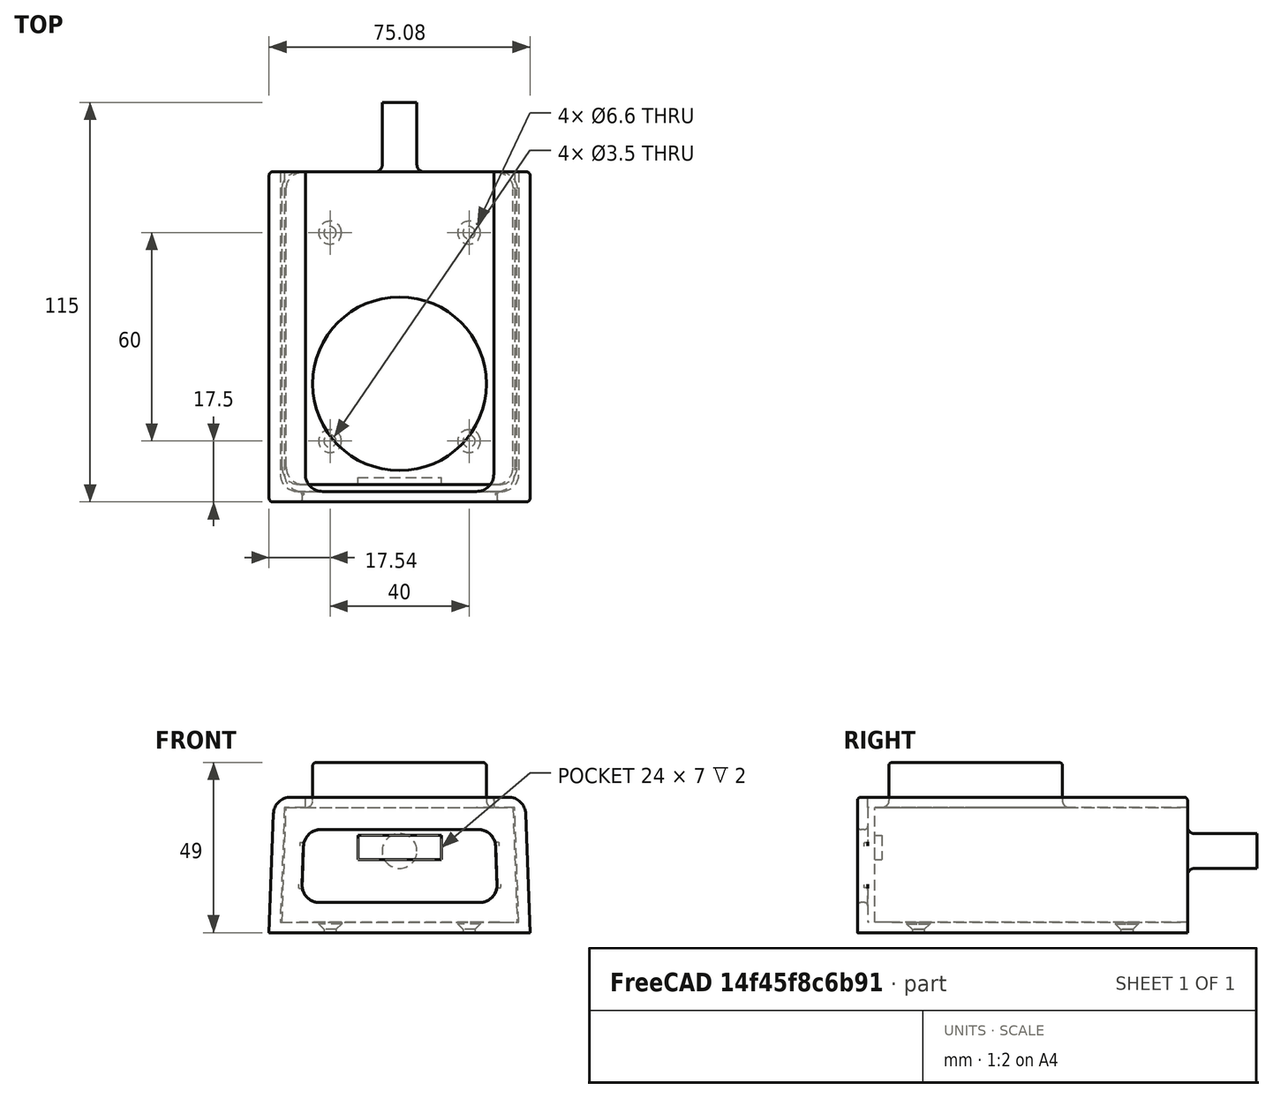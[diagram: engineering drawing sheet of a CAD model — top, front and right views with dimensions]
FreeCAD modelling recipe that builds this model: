
FCSTD DOCUMENT  (FreeCAD 0.22R37100 (Git))
Label: Tågvirke Mount
License: All rights reserved
LicenseURL: http://en.wikipedia.org/wiki/All_rights_reserved
objects: TechDraw::DrawViewDimension×9, Sketcher::SketchObject×7, PartDesign::Fillet×6, PartDesign::Pad×5, TechDraw::DrawViewPart×3, PartDesign::Body×2, PartDesign::SubShapeBinder×2, PartDesign::Pocket×1, PartDesign::Hole×1, TechDraw::DrawSVGTemplate×1, TechDraw::DrawViewImage×1, TechDraw::DrawPage×1
note: 53 computed .brp shape members not serialized (recipe doc carries the construction recipe); baked Part::Feature solids carry a one-line shape summary decoded from their .brp

FEATURE [Sketcher::SketchObject] Sketch
  AttachmentSupport = -> [XZ_Plane]
  FullyConstrained = true
  MapMode = 5
  Placement = pos=(0,0,0) rot=(1,0,0;1.5708rad)
  sketch-geometry (4):
    g0: LineSegment StartX=-32.625 StartY=33 StartZ=0 EndX=32.625 EndY=33 EndZ=0
    g1: LineSegment StartX=32.625 StartY=33 StartZ=0 EndX=33.825 EndY=1e-15 EndZ=0
    g2: LineSegment StartX=33.825 StartY=1e-15 StartZ=0 EndX=-33.825 EndY=0 EndZ=0
    g3: LineSegment StartX=-33.825 StartY=0 StartZ=0 EndX=-32.625 EndY=33 EndZ=0
  constraints (10):
    c: Coincident(g0,g1)
    c: Coincident(g1,g2)
    c: Coincident(g2,g3)
    c: Coincident(g3,g0)
    c: PointOnObject(g1,g-1)
    c: Symmetric(g0,g0,g-2)
    c: DistanceX(g0,g0) = 65.25
    c: DistanceX(g2,g2) = 67.65
    c: Symmetric(g2,g1,g-2)
    c: DistanceY(g1,g0) = 33
FEATURE [PartDesign::Pad] Pad
  Direction = (0,-1,2e-16)
  Length = 90
  Length2 = 10
  Placement = pos=(0,0,0) rot=(1,0,0;1.5708rad)
  Profile = -> Sketch
  ReferenceAxis = -> Sketch [N_Axis]
  Reversed = true
  Suppressed = false
  Type = 0
FEATURE [Sketcher::SketchObject] Sketch001
  AttachmentSupport = -> [Pad]
  FullyConstrained = true
  MapMode = 5
  Placement = pos=(0,0,0) rot=(1,0,0;1.5708rad)
  sketch-geometry (4):
    g0: LineSegment StartX=-12 StartY=25 StartZ=0 EndX=12 EndY=25 EndZ=0
    g1: LineSegment StartX=12 StartY=25 StartZ=0 EndX=12 EndY=18 EndZ=0
    g2: LineSegment StartX=12 StartY=18 StartZ=0 EndX=-12 EndY=18 EndZ=0
    g3: LineSegment StartX=-12 StartY=18 StartZ=0 EndX=-12 EndY=25 EndZ=0
  constraints (11):
    c: Coincident(g0,g1)
    c: Coincident(g1,g2)
    c: Coincident(g2,g3)
    c: Coincident(g3,g0)
    c: Horizontal(g2)
    c: Vertical(g1)
    c: Vertical(g3)
    c: DistanceX(g0,g0) = 24
    c: DistanceY(g1,g1) = 7
    c: Symmetric(g0,g0,g-2)
    c: DistanceY(g-1,g1) = 18
FEATURE [PartDesign::Pocket] Pocket
  BaseFeature = -> Pad
  Direction = (0,1,-2e-16)
  Length = 2
  Length2 = 5
  Placement = pos=(0,0,0) rot=(1,0,0;1.5708rad)
  Profile = -> Sketch001
  ReferenceAxis = -> Sketch001 [N_Axis]
  Suppressed = false
  Type = 0
FEATURE [Sketcher::SketchObject] Sketch002
  AttachmentSupport = -> [Pocket]
  FullyConstrained = true
  MapMode = 5
  Placement = pos=(0,1.45e-14,33) rot=(0,0,1;3.14159rad)
  sketch-geometry (1):
    g0: Circle CenterX=0 CenterY=-29 CenterZ=0 NormalX=0 NormalY=0 NormalZ=1 AngleXU=0 Radius=25
  constraints (3):
    c: PointOnObject(g0,g-2)
    c: Diameter(g0) = 50
    c: DistanceY(g0,g-1) = 29
FEATURE [PartDesign::Pad] Pad001
  BaseFeature = -> Pocket
  Direction = (0,2e-16,1)
  Length = 13
  Length2 = 10
  Placement = pos=(0,0,0) rot=(1,0,0;1.5708rad)
  Profile = -> Sketch002
  ReferenceAxis = -> Sketch002 [N_Axis]
  Suppressed = false
  Type = 0
FEATURE [PartDesign::Fillet] Fillet
  Base = -> Pad001 [Edge19]
  BaseFeature = -> Pad001
  Placement = pos=(0,0,0) rot=(1,0,0;1.5708rad)
  Radius = 1
  SupportTransform = false
  Suppressed = false
  UseAllEdges = false
FEATURE [PartDesign::Fillet] Fillet001
  Base = -> Fillet [Edge3]
  BaseFeature = -> Fillet
  Placement = pos=(0,0,0) rot=(1,0,0;1.5708rad)
  Radius = 2
  SupportTransform = false
  Suppressed = false
  UseAllEdges = false
FEATURE [PartDesign::Fillet] Fillet002
  Base = -> Fillet001 [Edge15,Edge21,Edge13,Edge14]
  BaseFeature = -> Fillet001
  Placement = pos=(0,0,0) rot=(1,0,0;1.5708rad)
  Radius = 5
  SupportTransform = false
  Suppressed = false
  UseAllEdges = false
FEATURE [Sketcher::SketchObject] Sketch003
  AttachmentSupport = -> [Fillet002]
  FullyConstrained = true
  MapMode = 5
  Placement = pos=(0,90,-1.98e-14) rot=(-1,0,0;1.5708rad)
  sketch-geometry (1):
    g0: Circle CenterX=0 CenterY=-20.5 CenterZ=0 NormalX=0 NormalY=0 NormalZ=1 AngleXU=0 Radius=5
  constraints (3):
    c: PointOnObject(g0,g-2)
    c: Diameter(g0) = 10
    c: DistanceY(g0,g-1) = 20.5
FEATURE [PartDesign::Pad] Pad002
  BaseFeature = -> Fillet002
  Direction = (0,1,-2e-16)
  Length = 20
  Length2 = 10
  Placement = pos=(0,0,0) rot=(1,0,0;1.5708rad)
  Profile = -> Sketch003
  ReferenceAxis = -> Sketch003 [N_Axis]
  Suppressed = false
  Type = 0
FEATURE [PartDesign::Fillet] Fillet003
  Base = -> Pad002 [Edge25]
  BaseFeature = -> Pad002
  Placement = pos=(0,0,0) rot=(1,0,0;1.5708rad)
  Radius = 2
  SupportTransform = false
  Suppressed = false
  UseAllEdges = false
FEATURE [PartDesign::Body] Body  label="Tågvirke"
  Group = -> [Sketch,Pad,Sketch001,Pocket,Sketch002,Pad001,Fillet,Fillet001,Fillet002,Sketch003,Pad002,Fillet003]
  Origin = -> Origin
  Tip = -> Fillet003
FEATURE [PartDesign::SubShapeBinder] Binder  label="Port Binder"
  BindCopyOnChange = 0
  BindMode = 0
  ClaimChildren = false
  Context = -> Body001 [Binder.]
  Fuse = false
  MakeFace = true
  OffsetFill = false
  OffsetIntersection = false
  OffsetJoinType = 0
  OffsetOpenResult = false
  PartialLoad = false
  Relative = true
  Support = -> [Body[Fillet001.Face7]]
  _Version = 2
FEATURE [PartDesign::SubShapeBinder] Binder001  label="Top Binder"
  BindCopyOnChange = 0
  BindMode = 0
  ClaimChildren = false
  Context = -> Body001 [Binder001.]
  Fuse = false
  MakeFace = true
  OffsetFill = false
  OffsetIntersection = false
  OffsetJoinType = 0
  OffsetOpenResult = false
  PartialLoad = false
  Relative = true
  Support = -> [Body[Fillet001.Face4]]
  _Version = 2
FEATURE [Sketcher::SketchObject] Sketch004  label="side_walls"
  AttachmentSupport = -> [XZ_Plane001]
  ExternalGeometry = -> [Binder]
  FullyConstrained = true
  MapMode = 5
  Placement = pos=(0,0,0) rot=(1,0,0;1.5708rad)
  expr: Constraints[27] = .Constraints.wall_thickness
  expr: Constraints[30] = .Constraints.wall_thickness
  sketch-geometry (12):
    g0: LineSegment StartX=-27.125 StartY=33 StartZ=0 EndX=-33.125 EndY=33 EndZ=0
    g1: LineSegment StartX=-33.125 StartY=33 StartZ=0 EndX=-34.325 EndY=1e-15 EndZ=0
    g2: LineSegment StartX=-34.325 StartY=1e-15 StartZ=0 EndX=34.325 EndY=0 EndZ=0
    g3: LineSegment StartX=34.325 StartY=0 StartZ=0 EndX=33.125 EndY=33 EndZ=0
    g4: LineSegment StartX=33.125 StartY=33 StartZ=0 EndX=27.125 EndY=33 EndZ=0
    g5: LineSegment StartX=-27.125 StartY=33 StartZ=0 EndX=-27.125 EndY=36 EndZ=0
    g6: LineSegment StartX=-27.125 StartY=36 StartZ=0 EndX=-36.125 EndY=36 EndZ=0
    g7: LineSegment StartX=-36.125 StartY=36 StartZ=0 EndX=-37.5432 EndY=-3 EndZ=0
    g8: LineSegment StartX=-37.5432 StartY=-3 StartZ=0 EndX=37.5432 EndY=-3 EndZ=0
    g9: LineSegment StartX=37.5432 StartY=-3 StartZ=0 EndX=36.125 EndY=36 EndZ=0
    g10: LineSegment StartX=36.125 StartY=36 StartZ=0 EndX=27.125 EndY=36 EndZ=0
    g11: LineSegment StartX=27.125 StartY=36 StartZ=0 EndX=27.125 EndY=33 EndZ=0
  constraints (31):
    c: Horizontal(g0)
    c: Coincident(g1,g2)
    c: Coincident(g2,g3)
    c: Coincident(g3,g4)
    c: DistanceX(g1,g-4) = 0.5  'Back Side Gap'
    c: Symmetric(g1,g2,g-2)
    c: DistanceX(g0,g-5) = 0.5  'Top Side Gap'
    c: Coincident(g0,g1)
    c: Symmetric(g0,g4,g-2)
    c: Symmetric(g0,g3,g-2)
    c: DistanceY(g-5,g0) = 0  'Outter Gap'
    c: DistanceY(g1,g-5) = 0  'Inner Gap'
    c: DistanceX(g0,g0) = 6  'Outter Catch'
    c: Coincident(g0,g5)
    c: Vertical(g5)
    c: Coincident(g5,g6)
    c: Horizontal(g6)
    c: Coincident(g6,g7)
    c: Coincident(g7,g8)
    c: Coincident(g8,g9)
    c: Coincident(g9,g10)
    c: Horizontal(g10)
    c: Coincident(g10,g11)
    c: Coincident(g11,g4)
    c: Vertical(g11)
    c: Symmetric(g9,g6,g-2)
    c: Symmetric(g7,g8,g-2)
    c: DistanceX(g3,g9) = 3
    c: Parallel(g3,g9)
    c: DistanceY(g4,g10) = 3  'wall_thickness'
    c: DistanceY(g8,g2) = 3
FEATURE [PartDesign::Pad] Pad003  label="Side Walls Pad"
  Direction = (0,-1,-2e-16)
  Length = 90
  Length2 = 2
  Placement = pos=(0,0,0) rot=(1,0,0;1.5708rad)
  Profile = -> Sketch004
  ReferenceAxis = -> Sketch004 [N_Axis]
  Reversed = true
  Suppressed = false
  Type = 4
FEATURE [Sketcher::SketchObject] Sketch005  label="end_plate"
  AttachmentSupport = -> [Pad003]
  ExternalGeometry = -> [Pad003]
  FullyConstrained = true
  MapMode = 5
  Placement = pos=(0,-2,-4e-16) rot=(1,0,0;1.5708rad)
  sketch-geometry (11):
    g0: LineSegment StartX=36.125 StartY=36 StartZ=0 EndX=37.5432 EndY=-3 EndZ=0
    g1: LineSegment StartX=37.5432 StartY=-3 StartZ=0 EndX=-37.5432 EndY=-3 EndZ=0
    g2: LineSegment StartX=-37.5432 StartY=-3 StartZ=0 EndX=-36.125 EndY=36 EndZ=0
    g3: LineSegment StartX=-28.2282 StartY=5.66127 StartZ=0 EndX=28.2282 EndY=5.66127 EndZ=0
    g4: LineSegment StartX=28.2282 StartY=5.66127 StartZ=0 EndX=37.5432 EndY=-3 EndZ=0
    g5: LineSegment StartX=-27.4637 StartY=26.685 StartZ=0 EndX=-28.2282 EndY=5.66127 EndZ=0
    g6: LineSegment StartX=28.2282 StartY=5.66127 StartZ=0 EndX=27.4637 EndY=26.685 EndZ=0
    g7: LineSegment StartX=-27.4637 StartY=26.685 StartZ=0 EndX=27.4637 EndY=26.685 EndZ=0
    g8: LineSegment StartX=36.125 StartY=36 StartZ=0 EndX=27.4637 EndY=26.685 EndZ=0
    g9: LineSegment StartX=-36.125 StartY=36 StartZ=0 EndX=36.125 EndY=36 EndZ=0
    g10: LineSegment StartX=27.125 StartY=36 StartZ=0 EndX=27.4637 EndY=26.685 EndZ=0
  constraints (25):
    c: Coincident(g0,g-6)
    c: Coincident(g0,g1)
    c: Coincident(g1,g-7)
    c: Coincident(g1,g2)
    c: Coincident(g5,g3)
    c: Horizontal(g3)
    c: Coincident(g3,g6)
    c: Coincident(g4,g3)
    c: Coincident(g4,g0)
    c: Angle(g0,g4) = 0.785398
    c: Parallel(g5,g2)
    c: Parallel(g6,g0)
    c: Coincident(g7,g6)
    c: Coincident(g8,g0)
    c: Coincident(g8,g6)
    c: Angle(g8,g0) = 0.785398
    c: Coincident(g5,g7)
    c: Coincident(g9,g2)
    c: Coincident(g9,g0)
    c: Coincident(g2,g-7)
    c: Coincident(g0,g-5)
    c: Coincident(g10,g-4)
    c: Coincident(g10,g6)
    c: Parallel(g10,g0)
    c: Symmetric(g5,g6,g-2)
FEATURE [PartDesign::Pad] Pad004  label="End Plate Pad"
  BaseFeature = -> Pad003
  Direction = (0,-1,-2e-16)
  Length = 3
  Length2 = 10
  Placement = pos=(0,0,0) rot=(1,0,0;1.5708rad)
  Profile = -> Sketch005
  ReferenceAxis = -> Sketch005 [N_Axis]
  Suppressed = false
  Type = 0
FEATURE [Sketcher::SketchObject] Sketch006  label="screw_holes"
  AttachmentSupport = -> [Pad004]
  ExternalGeometry = -> [Pad004]
  FullyConstrained = true
  MapMode = 5
  Placement = pos=(0,0,6e-16) rot=(0,0,1;3.14159rad)
  sketch-geometry (12):
    g0: Circle CenterX=-20 CenterY=-12.5 CenterZ=0 NormalX=0 NormalY=0 NormalZ=1 AngleXU=0 Radius=2
    g1: LineSegment StartX=-20 StartY=-12.5 StartZ=0 EndX=20 EndY=-12.5 EndZ=0
    g2: LineSegment StartX=20 StartY=-12.5 StartZ=0 EndX=20 EndY=-72.5 EndZ=0
    g3: LineSegment StartX=20 StartY=-72.5 StartZ=0 EndX=-20 EndY=-72.5 EndZ=0
    g4: LineSegment StartX=-20 StartY=-72.5 StartZ=0 EndX=-20 EndY=-12.5 EndZ=0
    g5: Circle CenterX=20 CenterY=-12.5 CenterZ=0 NormalX=0 NormalY=0 NormalZ=1 AngleXU=0 Radius=2
    g6: Circle CenterX=20 CenterY=-72.5 CenterZ=0 NormalX=0 NormalY=0 NormalZ=1 AngleXU=0 Radius=2
    g7: Circle CenterX=-20 CenterY=-72.5 CenterZ=0 NormalX=0 NormalY=0 NormalZ=1 AngleXU=0 Radius=2
    g8: GeomPoint X=0 Y=-42.5 Z=0
    g9: GeomPoint X=0 Y=5 Z=0
    g10: GeomPoint X=0 Y=-90 Z=0
    g11: LineSegment StartX=20 StartY=-42.5 StartZ=0 EndX=-20 EndY=-42.5 EndZ=0
  constraints (27):
    c: Diameter(g0) = 4
    c: Coincident(g1,g2)
    c: Coincident(g2,g3)
    c: Coincident(g3,g4)
    c: Coincident(g4,g1)
    c: Horizontal(g3)
    c: Vertical(g2)
    c: Vertical(g4)
    c: Coincident(g0,g1)
    c: Coincident(g5,g1)
    c: Coincident(g6,g2)
    c: Coincident(g7,g3)
    c: Symmetric(g0,g5,g-2)
    c: Equal(g0,g5)
    c: Equal(g5,g6)
    c: Equal(g6,g7)
    c: DistanceX(g1,g1) = 40
    c: DistanceY(g2,g2) = 60
    c: PointOnObject(g8,g-2)
    c: PointOnObject(g9,g-3)
    c: PointOnObject(g9,g-2)
    c: PointOnObject(g10,g-4)
    c: Symmetric(g10,g9,g8)
    c: Horizontal(g11)
    c: PointOnObject(g8,g11)
    c: PointOnObject(g11,g4)
    c: Symmetric(g5,g6,g11)
FEATURE [PartDesign::Hole] Hole  label="Holes"
  BaseFeature = -> Pad004
  CustomThreadClearance = 0
  Depth = 256.977
  DepthType = 1
  Diameter = 3.5
  DrillForDepth = false
  DrillPoint = 1
  DrillPointAngle = 118
  HoleCutCountersinkAngle = 90
  HoleCutCustomValues = false
  HoleCutDepth = 0.5
  HoleCutDiameter = 6.6
  HoleCutType = 3
  ModelThread = false
  Placement = pos=(0,0,0) rot=(1,0,0;1.5708rad)
  Profile = -> Sketch006
  Suppressed = false
  Tapered = true
  TaperedAngle = 90
  ThreadClass = 0
  ThreadDepth = 256.977
  ThreadDepthType = 0
  ThreadDirection = 0
  ThreadFit = 0
  ThreadSize = 0
  ThreadType = 0
  Threaded = false
  UseCustomThreadClearance = false
FEATURE [PartDesign::Fillet] Fillet004  label="Large Fillets"
  Base = -> Hole [Edge29,Edge39,Edge56,Edge58,Edge54,Edge53,Edge22,Edge10,Edge7,Edge24]
  BaseFeature = -> Hole
  Placement = pos=(0,0,0) rot=(1,0,0;1.5708rad)
  Radius = 5
  SupportTransform = false
  Suppressed = false
  UseAllEdges = false
FEATURE [PartDesign::Fillet] Fillet005  label="Small Fillets"
  Base = -> Fillet004 [Edge20,Edge16,Edge98,Edge110,Edge77,Edge94,Edge39]
  BaseFeature = -> Fillet004
  Placement = pos=(0,0,0) rot=(1,0,0;1.5708rad)
  Radius = 1
  SupportTransform = false
  Suppressed = false
  UseAllEdges = false
FEATURE [PartDesign::Body] Body001  label="Mount"
  Group = -> [Binder,Binder001,Sketch004,Pad003,Sketch005,Pad004,Sketch006,Hole,Fillet004,Fillet005]
  Origin = -> Origin001
  Tip = -> Fillet005
FEATURE [TechDraw::DrawSVGTemplate] Template
  Height = 210
  Orientation = 1
  Template = /Applications/FreeCAD.app/Contents/Resources/share/Mod/TechDraw/Templates/A4_Landscape_blank.svg
  Width = 297
FEATURE [TechDraw::DrawViewPart] View  label="Bottom"
  CoarseView = false
  Direction = (0,-1,0)
  Focus = 100
  HardHidden = false
  IsoCount = 0
  IsoHidden = false
  IsoVisible = false
  LockPosition = false
  Perspective = false
  Rotation = 0
  ScaleType = 0
  ScrubCount = 0
  SeamHidden = false
  SeamVisible = false
  SmoothHidden = false
  SmoothVisible = true
  Source = -> [Fillet005]
  X = 58.4217
  XDirection = (1,0,0)
  Y = 53.6321
FEATURE [TechDraw::DrawViewPart] View001  label="Back"
  CoarseView = false
  Direction = (0,0,1)
  Focus = 100
  HardHidden = false
  IsoCount = 0
  IsoHidden = false
  IsoVisible = false
  LockPosition = false
  Perspective = false
  Rotation = 0
  ScaleType = 0
  ScrubCount = 0
  SeamHidden = false
  SeamVisible = false
  SmoothHidden = false
  SmoothVisible = true
  Source = -> [Fillet005]
  X = 248.33
  XDirection = (1,0,0)
  Y = 81.2389
FEATURE [TechDraw::DrawViewPart] View002  label="Side"
  CoarseView = false
  Direction = (1,0,0)
  Focus = 100
  HardHidden = false
  IsoCount = 0
  IsoHidden = false
  IsoVisible = false
  LockPosition = false
  Perspective = false
  Rotation = 0
  ScaleType = 0
  ScrubCount = 0
  SeamHidden = false
  SeamVisible = false
  SmoothHidden = false
  SmoothVisible = true
  Source = -> [Fillet005]
  X = 150.898
  XDirection = (0,1,0)
  Y = 53.3126
FEATURE [TechDraw::DrawViewDimension] Dimension
  AngleOverride = false
  Arbitrary = false
  ArbitraryTolerances = false
  BoxCorners = (2) [(-37.5432,-19.5,-1e-07),(37.5432,19.5,1e-07)]
  EqualTolerance = true
  ExtensionAngle = 0
  FormatSpec = %.2w
  FormatSpecOverTolerance = %+.2w
  FormatSpecUnderTolerance = %+.2w
  Inverted = false
  LineAngle = 0
  LockPosition = false
  MeasureType = 1
  OverTolerance = 0
  References2D = -> [View]
  Rotation = 0
  ScaleType = 0
  TheoreticalExact = false
  Type = 1
  UnderTolerance = 0
  X = -1.5857
  Y = -31.9096
FEATURE [TechDraw::DrawViewDimension] Dimension001
  AngleOverride = false
  Arbitrary = false
  ArbitraryTolerances = false
  BoxCorners = (2) [(-37.5432,-19.5,-1e-07),(37.5432,19.5,1e-07)]
  EqualTolerance = true
  ExtensionAngle = 0
  FormatSpec = ⌀%.2w
  FormatSpecOverTolerance = %+.2w
  FormatSpecUnderTolerance = %+.2w
  Inverted = false
  LineAngle = 0
  LockPosition = false
  MeasureType = 1
  OverTolerance = 0
  References2D = -> [View]
  Rotation = 0
  ScaleType = 0
  TheoreticalExact = false
  Type = 5
  UnderTolerance = 0
  X = -39.8075
  Y = 32.2596
FEATURE [TechDraw::DrawViewDimension] Dimension002
  AngleOverride = false
  Arbitrary = false
  ArbitraryTolerances = false
  BoxCorners = (2) [(-37.5432,-19.5,-1e-07),(37.5432,19.5,1e-07)]
  EqualTolerance = true
  ExtensionAngle = 0
  FormatSpec = %.2w
  FormatSpecOverTolerance = %+.2w
  FormatSpecUnderTolerance = %+.2w
  Inverted = false
  LineAngle = 0
  LockPosition = false
  MeasureType = 1
  OverTolerance = 0
  References2D = -> [View]
  Rotation = 0
  ScaleType = 0
  TheoreticalExact = false
  Type = 2
  UnderTolerance = 0
  X = -47.1899
  Y = 1.69222
FEATURE [TechDraw::DrawViewDimension] Dimension003
  AngleOverride = false
  Arbitrary = false
  ArbitraryTolerances = false
  BoxCorners = (2) [(-37.5432,-19.5,-1e-07),(37.5432,19.5,1e-07)]
  EqualTolerance = true
  ExtensionAngle = 0
  FormatSpec = %.2w
  FormatSpecOverTolerance = %+.2w
  FormatSpecUnderTolerance = %+.2w
  Inverted = false
  LineAngle = 0
  LockPosition = false
  MeasureType = 1
  OverTolerance = 0
  References2D = -> [View]
  Rotation = 0
  ScaleType = 0
  TheoreticalExact = false
  Type = 1
  UnderTolerance = 0
  X = -0.281797
  Y = 31.6097
FEATURE [TechDraw::DrawViewDimension] Dimension005
  AngleOverride = false
  Arbitrary = false
  ArbitraryTolerances = false
  BoxCorners = (2) [(-37.5432,-47.5,-1e-07),(37.5432,47.5,1e-07)]
  EqualTolerance = true
  ExtensionAngle = 0
  FormatSpec = %.2w
  FormatSpecOverTolerance = %+.2w
  FormatSpecUnderTolerance = %+.2w
  Inverted = false
  LineAngle = 0
  LockPosition = false
  MeasureType = 1
  OverTolerance = 0
  References2D = -> [View001]
  Rotation = 0
  ScaleType = 0
  TheoreticalExact = false
  Type = 1
  UnderTolerance = 0
  X = -4.47904
  Y = 62.7954
FEATURE [TechDraw::DrawViewDimension] Dimension006
  AngleOverride = false
  Arbitrary = false
  ArbitraryTolerances = false
  BoxCorners = (2) [(-47.5,-19.5,-1e-07),(47.5,19.5,1e-07)]
  EqualTolerance = true
  ExtensionAngle = 0
  FormatSpec = %.2w
  FormatSpecOverTolerance = %+.2w
  FormatSpecUnderTolerance = %+.2w
  Inverted = false
  LineAngle = 0
  LockPosition = false
  MeasureType = 1
  OverTolerance = 0
  References2D = -> [View002]
  Rotation = 0
  ScaleType = 0
  TheoreticalExact = false
  Type = 2
  UnderTolerance = 0
  X = -55.6221
  Y = 3.57497
FEATURE [TechDraw::DrawViewDimension] Dimension007
  AngleOverride = false
  Arbitrary = false
  ArbitraryTolerances = false
  BoxCorners = (2) [(-47.5,-19.5,-1e-07),(47.5,19.5,1e-07)]
  EqualTolerance = true
  ExtensionAngle = 0
  FormatSpec = %.2w
  FormatSpecOverTolerance = %+.2w
  FormatSpecUnderTolerance = %+.2w
  Inverted = false
  LineAngle = 0
  LockPosition = false
  MeasureType = 1
  OverTolerance = 0
  References2D = -> [View002]
  Rotation = 0
  ScaleType = 0
  TheoreticalExact = false
  Type = 1
  UnderTolerance = 0
  X = -1.61245
  Y = 33.4491
FEATURE [TechDraw::DrawViewDimension] Dimension008
  AngleOverride = false
  Arbitrary = false
  ArbitraryTolerances = false
  BoxCorners = (2) [(-37.5432,-47.5,-1e-07),(37.5432,47.5,1e-07)]
  EqualTolerance = true
  ExtensionAngle = 0
  FormatSpec = ⌀%.2w
  FormatSpecOverTolerance = %+.2w
  FormatSpecUnderTolerance = %+.2w
  Inverted = false
  LineAngle = 0
  LockPosition = false
  MeasureType = 1
  OverTolerance = 0
  References2D = -> [View001]
  Rotation = 0
  ScaleType = 0
  TheoreticalExact = false
  Type = 5
  UnderTolerance = 0
  X = -5.38657
  Y = 43.3575
FEATURE [TechDraw::DrawViewImage] ActiveView001  label="ISO"
  Height = 100
  ImageFile = <userpath>/Library/Caches/FreeCAD/Cache/FreeCAD_Doc_7e5acf24-0245-4c81-aedd-a1b851715946_efeb40_20920/PageActiveView001rcCz4M.png
  LockPosition = false
  Rotation = 0
  Scale = 0.5
  ScaleType = 2
  Width = 100
  X = 103.232
  Y = 151.969
FEATURE [TechDraw::DrawViewDimension] Dimension009
  AngleOverride = false
  Arbitrary = false
  ArbitraryTolerances = false
  BoxCorners = (2) [(-37.5432,-47.5,-1e-07),(37.5432,47.5,1e-07)]
  EqualTolerance = true
  ExtensionAngle = 0
  FormatSpec = %.2w
  FormatSpecOverTolerance = %+.2w
  FormatSpecUnderTolerance = %+.2w
  Inverted = false
  LineAngle = 0
  LockPosition = false
  MeasureType = 1
  OverTolerance = 0
  References2D = -> [View001]
  Rotation = 0
  ScaleType = 0
  TheoreticalExact = false
  Type = 2
  UnderTolerance = 0
  X = -45.0784
  Y = 1.87563
FEATURE [TechDraw::DrawPage] Page
  KeepUpdated = true
  NextBalloonIndex = 1
  ProjectionType = 0
  Template = -> Template
  Views = -> [View,View001,View002,Dimension,Dimension001,Dimension002,Dimension003,Dimension005,Dimension006,Dimension007,Dimension008,ActiveView001,Dimension009]
